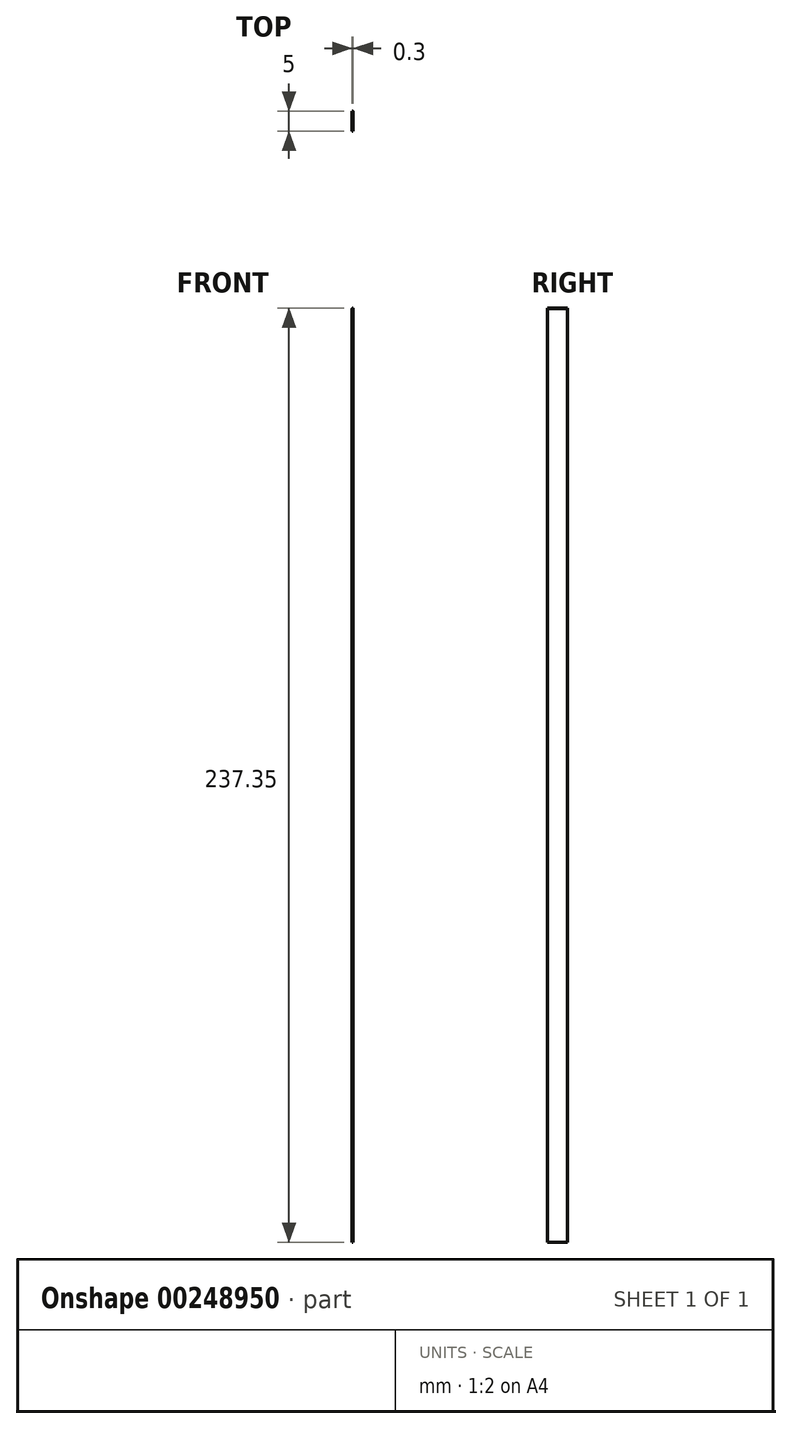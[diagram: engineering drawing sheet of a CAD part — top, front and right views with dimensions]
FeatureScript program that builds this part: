
annotation { "Feature Type Name" : "Feature", "Feature Type Description" : "" }
export const myFeature = defineFeature(function(context is Context, id is Id, definition is map)
    precondition{}
    {
        {
            var Q0;
            Q0=qCreatedBy(makeId("Front.planeOp"),FACE);
            var sketch = newSketch(context, id + "F0", { "sketchPlane" : qUnion([Q0])});
            skLineSegment(sketch, "E0.bottom", {"start": v(-36.48, 39.16) * mm, "end": v(-36.18, 39.16) * mm});
            skLineSegment(sketch, "E0.top", {"start": v(-36.48, -198.09) * mm, "end": v(-36.18, -198.09) * mm});
            skLineSegment(sketch, "E0.left", {"start": v(-36.18, 39.16) * mm, "end": v(-36.18, -198.09) * mm});
            skLineSegment(sketch, "E0.right", {"start": v(-36.48, 39.16) * mm, "end": v(-36.48, -198.09) * mm});
            skLineSegment(sketch, "E1", {"start": v(-36.48, 39.16) * mm, "end": v(-36.33, 39.16) * mm});
            skCircle(sketch, "E2", {"center": v(-36.33, 39.16) * mm, "radius": 0.1 * mm});
            skSolve(sketch);
        }
        {
            var Q0;
            {var subQ0=sQuery(id+"F0.wireOp",EDGE,"E1");var subQ1=sQuery(id+"F0.wireOp",EDGE,"E0.bottom");var subQ2=makeQuery(id+"F0.imprint","INTERSECT",VERTEX,{"derivedFrom":[subQ1,subQ0]});Q0=makeQuery(id+"F0.imprint","IMPRINT",FACE,{"disambiguationData":[TD([[makeQuery(id+"F0.imprint","IMPRINT",EDGE,{"disambiguationData":[TD([[subQ2,-1.0]])],"derivedFrom":subQ1}),1.0]])]});}
            var Q1;
            {var subQ0=sQuery(id+"F0.wireOp",EDGE,"E1");var subQ1=sQuery(id+"F0.wireOp",EDGE,"E0.bottom");var subQ2=makeQuery(id+"F0.imprint","INTERSECT",VERTEX,{"derivedFrom":[subQ1,subQ0]});Q1=makeQuery(id+"F0.imprint","IMPRINT",FACE,{"disambiguationData":[TD([[makeQuery(id+"F0.imprint","IMPRINT",EDGE,{"disambiguationData":[TD([[subQ2,-1.0]])],"derivedFrom":subQ1}),-1.0]])]});}
            var Q2;
            Q2=makeQuery(id+"F0.imprint","IMPRINT",FACE,{"disambiguationData":[TD([[makeQuery(id+"F0.imprint","IMPRINT",EDGE,{"derivedFrom":sQuery(id+"F0.wireOp",EDGE,"E0.top")}),1.0]])]});
            extrude(context, id + "F1", {"entities" : qUnion([Q0, Q1, Q2]), "depth" : 5 * mm});
        }
    });
